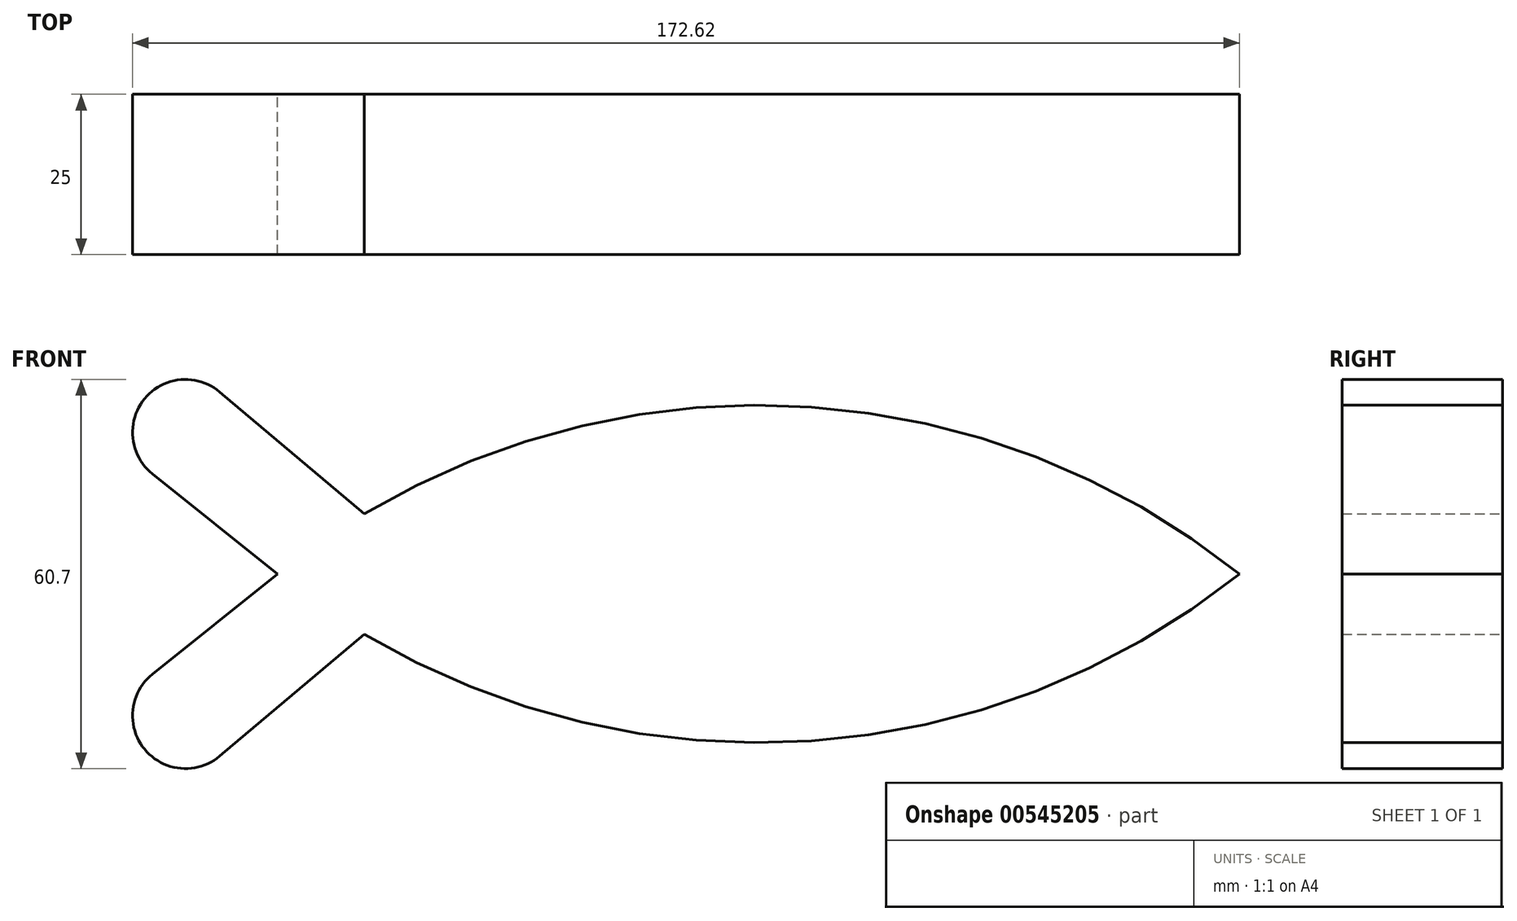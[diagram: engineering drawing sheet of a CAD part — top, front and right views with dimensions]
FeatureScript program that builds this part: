
annotation { "Feature Type Name" : "Feature", "Feature Type Description" : "" }
export const myFeature = defineFeature(function(context is Context, id is Id, definition is map)
    precondition{}
    {
        {
            var Q0;
            Q0=qCreatedBy(makeId("Front.planeOp"),FACE);
            var sketch = newSketch(context, id + "F0", { "sketchPlane" : qUnion([Q0])});
            skArc(sketch, "E0", {"start": v(150, 0) * mm, "mid": v(75, 26.33) * mm, "end": v(0, 0) * mm});
            skArc(sketch, "E1.MirrorCS", {"start": v(150, 0) * mm, "mid": v(75, -26.33) * mm, "end": v(0, 0) * mm});
            skLineSegment(sketch, "E2", {"start": v(0, 0) * mm, "end": v(-19.52, 15.62) * mm});
            skArc(sketch, "E3", {"start": v(-19.52, 15.62) * mm, "mid": v(-20.73, 27.34) * mm, "end": v(-9, 28.4) * mm});
            skLineSegment(sketch, "E4", {"start": v(-9, 28.4) * mm, "end": v(13.52, 9.38) * mm});
            skLineSegment(sketch, "E5.MirrorCS", {"start": v(-9, -28.4) * mm, "end": v(13.52, -9.38) * mm});
            skArc(sketch, "E6.MirrorCS", {"start": v(-19.52, -15.62) * mm, "mid": v(-20.73, -27.34) * mm, "end": v(-9, -28.4) * mm});
            skLineSegment(sketch, "E7.MirrorCS", {"start": v(0, 0) * mm, "end": v(-19.52, -15.62) * mm});
            skSolve(sketch);
        }
        {
            var Q0;
            Q0=qSketchRegion(id+"F0",true);
            extrude(context, id + "F1", {"entities" : qUnion([Q0]), "depth" : 25 * mm});
        }
    });
